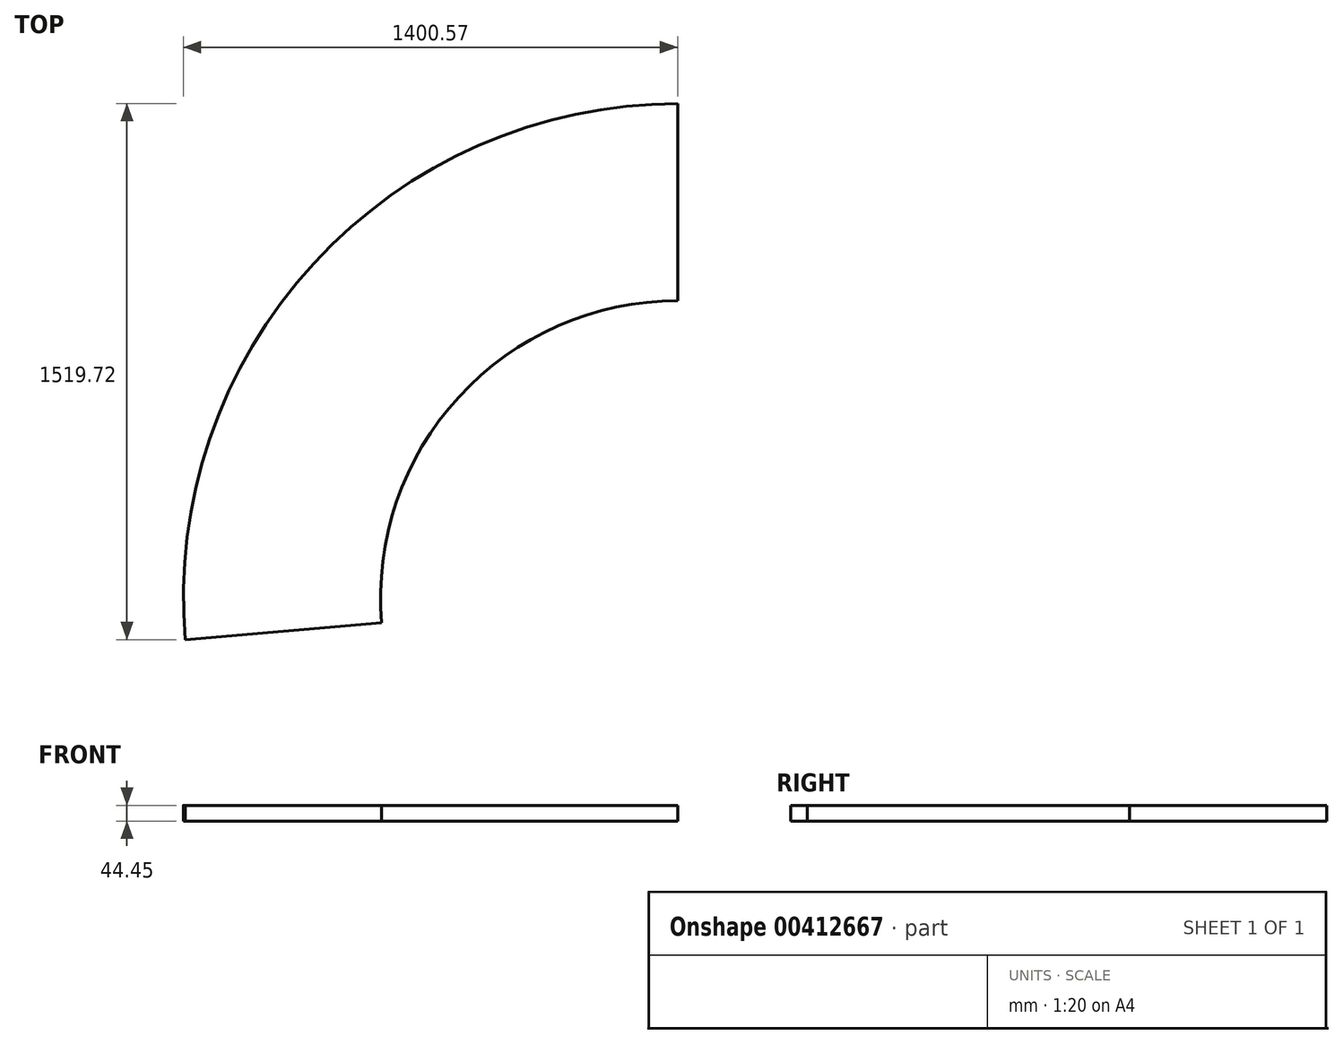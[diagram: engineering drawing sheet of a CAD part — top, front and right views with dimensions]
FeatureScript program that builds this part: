
annotation { "Feature Type Name" : "Feature", "Feature Type Description" : "" }
export const myFeature = defineFeature(function(context is Context, id is Id, definition is map)
    precondition{}
    {
        {
            var Q0;
            Q0=qCreatedBy(makeId("Top.planeOp"),FACE);
            var sketch = newSketch(context, id + "F0", { "sketchPlane" : qUnion([Q0])});
            skLineSegment(sketch, "E0", {"start": v(0, 0) * mm, "end": v(-2019.3, 0) * mm});
            skLineSegment(sketch, "E1", {"start": v(-2019.3, 0) * mm, "end": v(-2019.3, 3632.2) * mm});
            skLineSegment(sketch, "E2", {"start": v(-2019.3, 3632.2) * mm, "end": v(-546.1, 3632.2) * mm});
            skLineSegment(sketch, "E3", {"start": v(-546.1, 3632.2) * mm, "end": v(1076.15, 4476.48) * mm});
            skLineSegment(sketch, "E4", {"start": v(1076.15, 4476.48) * mm, "end": v(11356.8, 4476.48) * mm});
            skLineSegment(sketch, "E5", {"start": v(11356.8, 4476.48) * mm, "end": v(11356.8, -1705.24) * mm});
            skPoint(sketch, "E6", {"position": v(2295.35, 4476.48) * mm});
            skPoint(sketch, "E7", {"position": v(-5.35, 3913.63) * mm});
            skLineSegment(sketch, "E8", {"start": v(11017.08, 4476.48) * mm, "end": v(11017.08, 4432.03) * mm});
            skLineSegment(sketch, "E9", {"start": v(11017.08, 4432.03) * mm, "end": v(5305.25, 4432.03) * mm});
            skLineSegment(sketch, "E10", {"start": v(5305.25, 4432.03) * mm, "end": v(5305.25, 4476.48) * mm});
            skText(sketch, "E11", { "text": "Windows", "fontName": "OpenSans-Regular.ttf"});
            skLineSegment(sketch, "E12", {"start": v(11356.8, -1705.24) * mm, "end": v(11509.2, -1705.24) * mm});
            skLineSegment(sketch, "E13", {"start": v(11509.2, -1705.24) * mm, "end": v(11509.2, 4359) * mm});
            skLineSegment(sketch, "E14", {"start": v(11509.2, 4359) * mm, "end": v(13033.2, 4359) * mm});
            skLineSegment(sketch, "E15", {"start": v(13033.2, 4359) * mm, "end": v(13610.85, 3787.2) * mm});
            const initialGuessF0  = {"E11": [7.00887, 4.50742, 1, 0, 0.10207]};
            skSetInitialGuess(sketch, initialGuessF0);
            skSolve(sketch);
        }
        {
            var Q0;
            Q0=qCreatedBy(makeId("Top.planeOp"),FACE);
            var sketch = newSketch(context, id + "F1", { "sketchPlane" : qUnion([Q0])});
            skLineSegment(sketch, "E16", {"start": v(-50.8, 0) * mm, "end": v(-50.8, 693.42) * mm});
            skLineSegment(sketch, "E17", {"start": v(-50.8, 693.42) * mm, "end": v(-653.85, 892.3) * mm});
            skLineSegment(sketch, "E18.0", {"start": v(-1384.3, 1009.65) * mm, "end": v(-1384.3, 2622.55) * mm});
            skArc(sketch, "E19", {"start": v(-1384.3, 1009.65) * mm, "mid": v(-1069.07, 639.74) * mm, "end": v(-653.85, 892.3) * mm});
            skArc(sketch, "E20", {"start": v(-2019.3, 1009.65) * mm, "mid": v(-1169.8, 12.78) * mm, "end": v(-50.8, 693.42) * mm});
            skArc(sketch, "E21", {"start": v(-640.7, 2687.6) * mm, "mid": v(-1042.3, 2995.77) * mm, "end": v(-1384.3, 2622.55) * mm});
            skArc(sketch, "E22", {"start": v(-15.34, 2797.87) * mm, "mid": v(-1097.65, 3628.36) * mm, "end": v(-2019.3, 2622.55) * mm});
            skLineSegment(sketch, "E23", {"start": v(-2019.3, 2622.55) * mm, "end": v(-2019.3, 1009.65) * mm});
            skLineSegment(sketch, "E24", {"start": v(-15.34, 2797.87) * mm, "end": v(-640.7, 2687.6) * mm});
            skLineSegment(sketch, "E25.0", {"start": v(1456.08, 4400.28) * mm, "end": v(11356.8, 4400.28) * mm});
            skLineSegment(sketch, "E26.0", {"start": v(774.31, 4233.5) * mm, "end": v(1094.8, 4400.28) * mm, "construction": true});
            skArc(sketch, "E27", {"start": v(1456.08, 4400.28) * mm, "mid": v(368.33, 3922.34) * mm, "end": v(-15.34, 2797.87) * mm});
            skLineSegment(sketch, "E28", {"start": v(-15.34, 2797.87) * mm, "end": v(617.36, 2851.9) * mm});
            skArc(sketch, "E29.0", {"start": v(1456.08, 3765.28) * mm, "mid": v(836.05, 3492.85) * mm, "end": v(617.36, 2851.9) * mm});
            skLineSegment(sketch, "E30.0", {"start": v(6454.6, 3181.08) * mm, "end": v(7724.6, 3181.08) * mm});
            skLineSegment(sketch, "E31.0", {"start": v(11356.8, 4476.48) * mm, "end": v(11356.8, 133.08) * mm});
            skLineSegment(sketch, "E32.0", {"start": v(10137.6, 2901.68) * mm, "end": v(10137.6, 1631.68) * mm});
            skLineSegment(sketch, "E33.0", {"start": v(9223.2, 4400.28) * mm, "end": v(9223.2, 3181.08) * mm});
            skLineSegment(sketch, "E34.0", {"start": v(10137.6, 2266.68) * mm, "end": v(11356.8, 2266.68) * mm});
            skLineSegment(sketch, "E35.0", {"start": v(7089.6, 4400.28) * mm, "end": v(7089.6, 3181.08) * mm});
            skLineSegment(sketch, "E36.0", {"start": v(10137.6, 133.08) * mm, "end": v(11356.8, 133.08) * mm});
            skLineSegment(sketch, "E37", {"start": v(1456.08, 3765.28) * mm, "end": v(6022.8, 3765.28) * mm});
            skArc(sketch, "E38", {"start": v(6454.6, 3333.48) * mm, "mid": v(6328.13, 3638.8) * mm, "end": v(6022.8, 3765.28) * mm});
            skLineSegment(sketch, "E39", {"start": v(6454.6, 3333.48) * mm, "end": v(6454.6, 3181.08) * mm});
            skLineSegment(sketch, "E40", {"start": v(7724.6, 3181.08) * mm, "end": v(7724.6, 3333.48) * mm});
            skArc(sketch, "E41", {"start": v(8588.2, 3333.48) * mm, "mid": v(8156.4, 3765.28) * mm, "end": v(7724.6, 3333.48) * mm});
            skLineSegment(sketch, "E42", {"start": v(8588.2, 3333.48) * mm, "end": v(8588.2, 3181.08) * mm});
            skArc(sketch, "E43", {"start": v(9223.2, 3333.48) * mm, "mid": v(8156.4, 4400.28) * mm, "end": v(7089.6, 3333.48) * mm});
            skArc(sketch, "E44", {"start": v(7089.6, 3333.48) * mm, "mid": v(6777.14, 4087.82) * mm, "end": v(6022.8, 4400.28) * mm});
            skLineSegment(sketch, "E45.trimOffspring", {"start": v(8588.2, 3181.08) * mm, "end": v(9858.2, 3181.08) * mm});
            skArc(sketch, "E46", {"start": v(10290, 2266.68) * mm, "mid": v(11044.34, 4087.82) * mm, "end": v(9223.2, 3333.48) * mm});
            skArc(sketch, "E47.0", {"start": v(10290, 2901.68) * mm, "mid": v(10595.33, 3638.8) * mm, "end": v(9858.2, 3333.48) * mm});
            skLineSegment(sketch, "E48", {"start": v(10290, 2901.68) * mm, "end": v(10137.6, 2901.68) * mm});
            skLineSegment(sketch, "E49", {"start": v(9858.2, 3333.48) * mm, "end": v(9858.2, 3181.08) * mm});
            skLineSegment(sketch, "E50", {"start": v(10137.6, 1631.68) * mm, "end": v(10290, 1631.68) * mm});
            skArc(sketch, "E51", {"start": v(10290, 768.08) * mm, "mid": v(10721.8, 1199.88) * mm, "end": v(10290, 1631.68) * mm});
            skLineSegment(sketch, "E52", {"start": v(10290, 768.08) * mm, "end": v(10137.6, 768.08) * mm});
            skArc(sketch, "E53", {"start": v(10290, 133.08) * mm, "mid": v(11356.8, 1199.88) * mm, "end": v(10290, 2266.68) * mm});
            skLineSegment(sketch, "E54.trimOffspring", {"start": v(10137.6, 768.08) * mm, "end": v(10137.6, 133.08) * mm});
            skPoint(sketch, "E55.orphan", {"position": v(11356.8, -1705.24) * mm});
            skArc(sketch, "E56", {"start": v(13326.5, 4050.37) * mm, "mid": v(11589.37, 3697.95) * mm, "end": v(12576, 2225.4) * mm});
            skLineSegment(sketch, "E57", {"start": v(12576, 2225.4) * mm, "end": v(11509.2, 2225.4) * mm});
            skLineSegment(sketch, "E58.0", {"start": v(11509.2, -1705.24) * mm, "end": v(11509.2, 4359) * mm});
            skLineSegment(sketch, "E59.0", {"start": v(11509.2, 4359) * mm, "end": v(13033.2, 4359) * mm});
            skLineSegment(sketch, "E60.0", {"start": v(13033.2, 4359) * mm, "end": v(13610.85, 3787.2) * mm});
            skLineSegment(sketch, "E61", {"start": v(12576, 2225.4) * mm, "end": v(12728.4, 2225.4) * mm});
            skLineSegment(sketch, "E62", {"start": v(12728.4, 2225.4) * mm, "end": v(12728.4, 1590.4) * mm});
            skLineSegment(sketch, "E63", {"start": v(12728.4, 91.8) * mm, "end": v(11509.2, 91.8) * mm});
            skLineSegment(sketch, "E64", {"start": v(12728.4, 1590.4) * mm, "end": v(12576, 1590.4) * mm});
            skArc(sketch, "E65", {"start": v(12576, 1590.4) * mm, "mid": v(12144.2, 1158.6) * mm, "end": v(12576, 726.8) * mm});
            skLineSegment(sketch, "E66", {"start": v(12576, 726.8) * mm, "end": v(12728.4, 726.8) * mm});
            skArc(sketch, "E67", {"start": v(12576, 2225.4) * mm, "mid": v(11509.2, 1158.6) * mm, "end": v(12576, 91.8) * mm});
            skLineSegment(sketch, "E68.trimOffspring", {"start": v(12728.4, 726.8) * mm, "end": v(12728.4, 91.8) * mm});
            skLineSegment(sketch, "E69", {"start": v(12728.4, 2225.4) * mm, "end": v(12728.4, 2860.4) * mm});
            skLineSegment(sketch, "E70", {"start": v(12728.4, 2860.4) * mm, "end": v(12576, 2860.4) * mm});
            skArc(sketch, "E71", {"start": v(12879.77, 3599.08) * mm, "mid": v(12176.65, 3456.43) * mm, "end": v(12576, 2860.4) * mm});
            skLineSegment(sketch, "E72", {"start": v(13326.5, 4050.37) * mm, "end": v(12879.77, 3599.08) * mm});
            skLineSegment(sketch, "E73", {"start": v(1456.08, 4400.28) * mm, "end": v(1456.08, 3765.28) * mm});
            skLineSegment(sketch, "E74", {"start": v(6022.8, 4400.28) * mm, "end": v(6022.8, 3765.28) * mm});
            skLineSegment(sketch, "E75", {"start": v(8156.4, 3765.28) * mm, "end": v(8156.4, 4400.28) * mm});
            skLineSegment(sketch, "E76", {"start": v(3739.44, 4400.28) * mm, "end": v(3739.44, 3765.28) * mm});
            skLineSegment(sketch, "E77", {"start": v(-1384.3, 1009.65) * mm, "end": v(-2019.3, 1009.65) * mm});
            skLineSegment(sketch, "E78", {"start": v(-1384.3, 2622.55) * mm, "end": v(-2019.3, 2622.55) * mm});
            skLineSegment(sketch, "E79", {"start": v(12144.2, 1158.6) * mm, "end": v(11509.2, 1158.6) * mm});
            skLineSegment(sketch, "E80", {"start": v(10721.8, 1199.88) * mm, "end": v(11356.8, 1199.88) * mm});
            skLineSegment(sketch, "E81", {"start": v(11509.2, 3292.2) * mm, "end": v(12144.2, 3292.2) * mm});
            skLineSegment(sketch, "E82", {"start": v(10290, 4400.28) * mm, "end": v(10290, 3765.28) * mm});
            skLineSegment(sketch, "E83", {"start": v(11356.8, 3333.48) * mm, "end": v(10721.8, 3333.48) * mm});
            skLineSegment(sketch, "E84.0", {"start": v(0, 0) * mm, "end": v(-2019.3, 0) * mm});
            skLineSegment(sketch, "E84.1", {"start": v(-2019.3, 0) * mm, "end": v(-2019.3, 3632.2) * mm});
            skLineSegment(sketch, "E84.2", {"start": v(-2019.3, 3632.2) * mm, "end": v(-546.1, 3632.2) * mm});
            skLineSegment(sketch, "E84.3", {"start": v(-546.1, 3632.2) * mm, "end": v(1076.15, 4476.48) * mm});
            skLineSegment(sketch, "E84.4", {"start": v(1076.15, 4476.48) * mm, "end": v(11356.8, 4476.48) * mm});
            skLineSegment(sketch, "E84.5", {"start": v(11356.8, 4476.48) * mm, "end": v(11356.8, -1705.24) * mm});
            skPoint(sketch, "E84.6", {"position": v(2295.35, 4476.48) * mm});
            skPoint(sketch, "E84.7", {"position": v(-5.35, 3913.63) * mm});
            skLineSegment(sketch, "E84.8", {"start": v(11017.08, 4476.48) * mm, "end": v(11017.08, 4432.03) * mm});
            skLineSegment(sketch, "E84.9", {"start": v(11017.08, 4432.03) * mm, "end": v(5305.25, 4432.03) * mm});
            skLineSegment(sketch, "E84.10", {"start": v(5305.25, 4432.03) * mm, "end": v(5305.25, 4476.48) * mm});
            skLineSegment(sketch, "E84.11", {"start": v(11356.8, -1705.24) * mm, "end": v(11509.2, -1705.24) * mm});
            skSolve(sketch);
        }
        {
            var Q0;
            Q0=makeQuery(id+"F1.imprint","IMPRINT",FACE,{"disambiguationData":[TD([[makeQuery(id+"F1.imprint","IMPRINT",EDGE,{"derivedFrom":sQuery(id+"F1.wireOp",EDGE,"E27")}),1.0]])]});
            var sketch = newSketch(context, id + "F2", { "sketchPlane" : qUnion([Q0])});
            skArc(sketch, "E85.0.0", {"start": v(1456.08, 4400.28) * mm, "mid": v(368.33, 3922.34) * mm, "end": v(-15.34, 2797.87) * mm});
            skLineSegment(sketch, "E85.0.1", {"start": v(-15.34, 2797.87) * mm, "end": v(617.36, 2851.9) * mm});
            skArc(sketch, "E85.0.2", {"start": v(617.36, 2851.9) * mm, "mid": v(836.05, 3492.85) * mm, "end": v(1456.08, 3765.28) * mm});
            skLineSegment(sketch, "E85.0.3", {"start": v(1456.08, 3765.28) * mm, "end": v(1456.08, 4400.28) * mm});
            skArc(sketch, "E86.0", {"start": v(60.58, 2804.36) * mm, "mid": v(424.46, 3870.8) * mm, "end": v(1456.08, 4324.08) * mm});
            skSolve(sketch);
        }
        {
            var Q0;
            {var subQ0=sQuery(id+"F2.wireOp",EDGE,"E85.0.2");Q0=makeQuery(id+"F2.imprint","IMPRINT",FACE,{"disambiguationData":[TD([[makeQuery(id+"F2.imprint","IMPRINT",EDGE,{"derivedFrom":subQ0}),-1.0]])]});}
            extrude(context, id + "F3", {"entities" : qUnion([Q0]), "depth" : 44.45 * mm});
        }
    });
